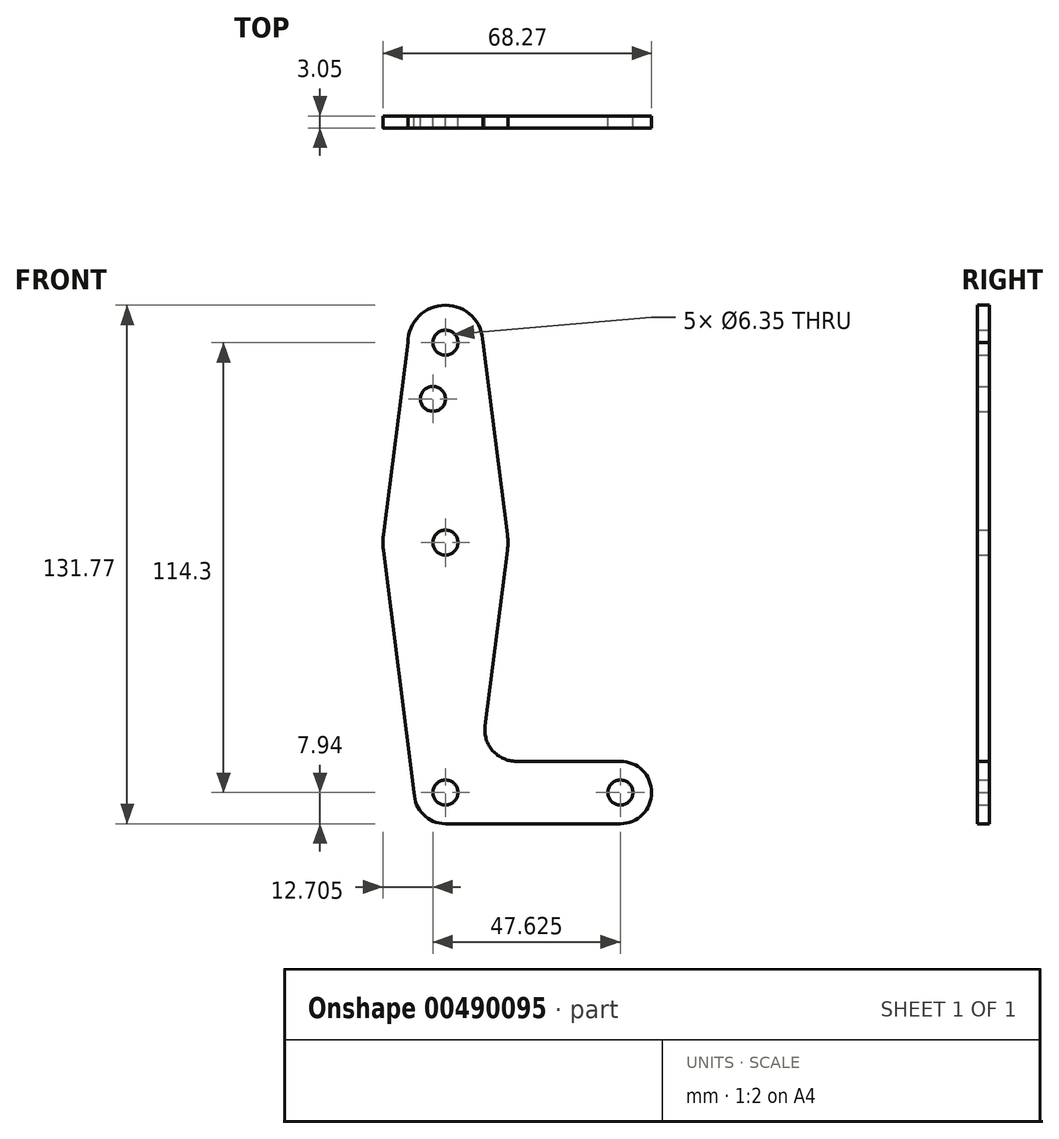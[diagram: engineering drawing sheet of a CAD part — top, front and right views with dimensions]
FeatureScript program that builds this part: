
annotation { "Feature Type Name" : "Feature", "Feature Type Description" : "" }
export const myFeature = defineFeature(function(context is Context, id is Id, definition is map)
    precondition{}
    {
        {
            var Q0;
            Q0=qCreatedBy(makeId("Front.planeOp"),FACE);
            var sketch = newSketch(context, id + "F0", { "sketchPlane" : qUnion([Q0])});
            skLineSegment(sketch, "E0", {"start": v(0, 0) * mm, "end": v(0, 114.3) * mm, "construction": true});
            skLineSegment(sketch, "E1", {"start": v(0, 0) * mm, "end": v(44.45, 0) * mm, "construction": true});
            skCircle(sketch, "E2", {"center": v(0, 114.3) * mm, "radius": 9.53 * mm});
            skCircle(sketch, "E3", {"center": v(0, 63.5) * mm, "radius": 15.88 * mm});
            skCircle(sketch, "E4", {"center": v(0, 0) * mm, "radius": 7.94 * mm});
            skCircle(sketch, "E5", {"center": v(44.45, 0) * mm, "radius": 7.94 * mm});
            skLineSegment(sketch, "E6", {"start": v(15.75, 65.5) * mm, "end": v(9.53, 114.3) * mm});
            skLineSegment(sketch, "E7", {"start": v(-9.52, 114.3) * mm, "end": v(-15.75, 65.5) * mm});
            skLineSegment(sketch, "E8", {"start": v(-7.94, 0) * mm, "end": v(-15.75, 61.5) * mm});
            skLineSegment(sketch, "E9", {"start": v(44.45, 7.94) * mm, "end": v(44.45, 7.94) * mm});
            skLineSegment(sketch, "E10", {"start": v(0, -7.94) * mm, "end": v(44.45, -7.94) * mm});
            skCircle(sketch, "E11", {"center": v(0, 114.3) * mm, "radius": 3.18 * mm});
            skCircle(sketch, "E12", {"center": v(0, 63.5) * mm, "radius": 3.18 * mm});
            skCircle(sketch, "E13", {"center": v(44.45, 0) * mm, "radius": 3.18 * mm});
            skCircle(sketch, "E14", {"center": v(-3.18, 100.03) * mm, "radius": 3.18 * mm});
            skPoint(sketch, "E15.end.orphan", {"position": v(15.75, 61.5) * mm});
            skLineSegment(sketch, "E16", {"start": v(15.75, 61.5) * mm, "end": v(10.08, 16.89) * mm});
            skLineSegment(sketch, "E17", {"start": v(44.45, 7.94) * mm, "end": v(17.97, 7.94) * mm});
            skPoint(sketch, "E18.newPointA", {"position": v(7.94, 0) * mm});
            skPoint(sketch, "E18.newPointB", {"position": v(0, 7.94) * mm});
            skArc(sketch, "E18.filletArc", {"start": v(10.08, 16.89) * mm, "mid": v(12, 10.63) * mm, "end": v(17.97, 7.94) * mm});
            skCircle(sketch, "E19", {"center": v(0, 0) * mm, "radius": 3.18 * mm});
            skSolve(sketch);
        }
        {
            var Q0;
            Q0 = qSketchRegion(id + "F0", true);
            extrude(context, id + "F1", {"entities" : qUnion([Q0]), "depth" : 3.05 * mm});
        }
    });
